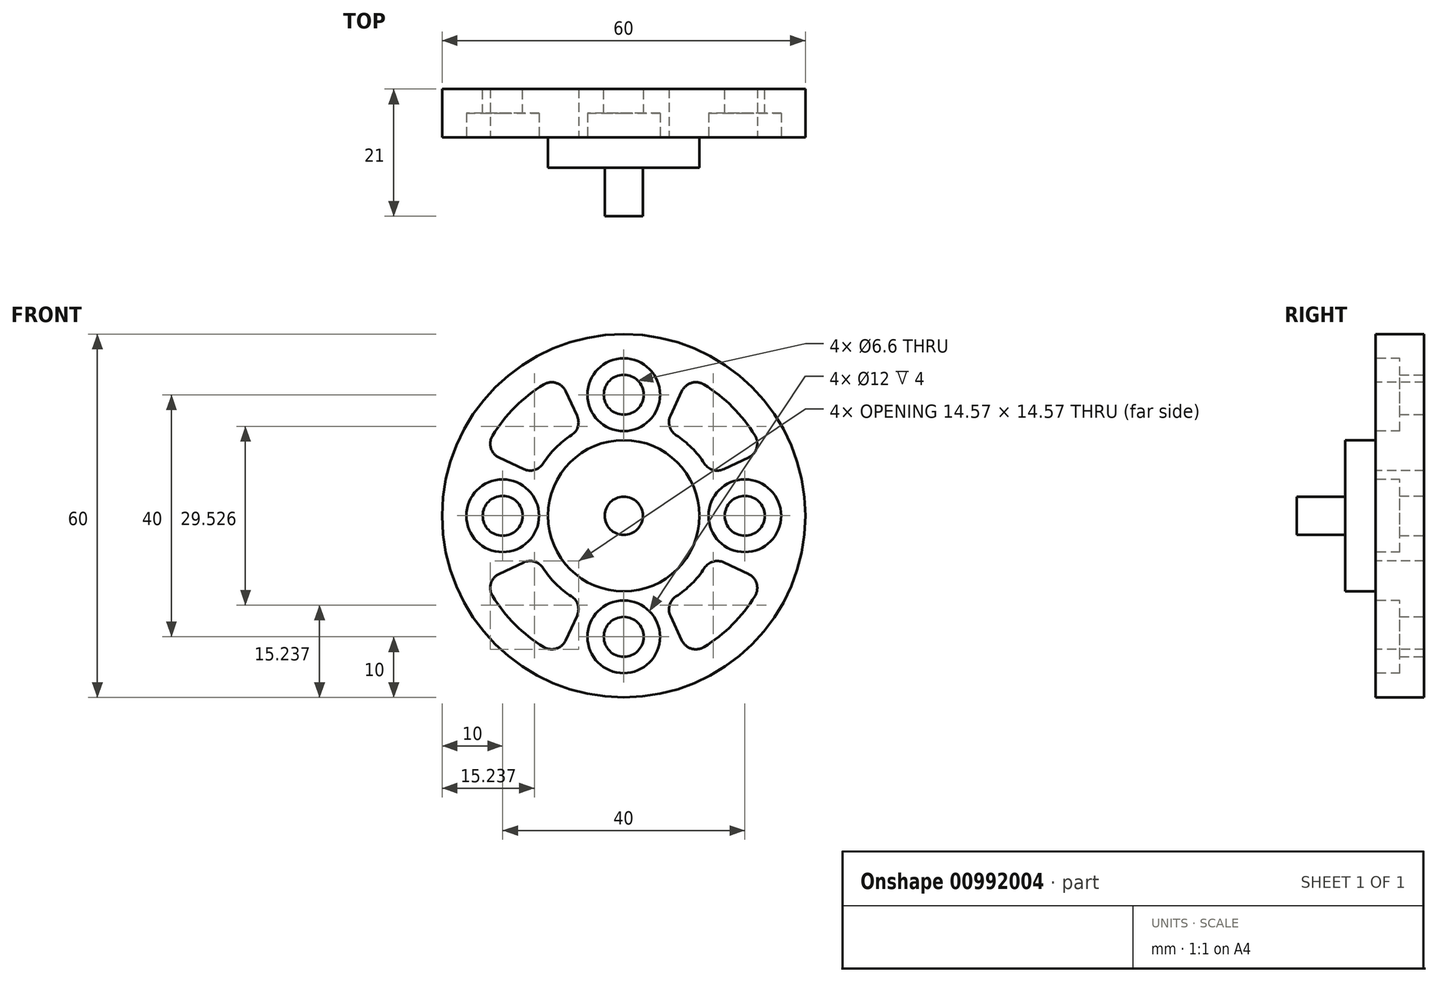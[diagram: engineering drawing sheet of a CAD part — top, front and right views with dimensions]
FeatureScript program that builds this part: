
annotation { "Feature Type Name" : "Feature", "Feature Type Description" : "" }
export const myFeature = defineFeature(function(context is Context, id is Id, definition is map)
    precondition{}
    {
        {
            var Q0;
            Q0=qCreatedBy(makeId("Front.planeOp"),FACE);
            var sketch = newSketch(context, id + "F0", { "sketchPlane" : qUnion([Q0])});
            skCircle(sketch, "E0", {"center": v(0, 0) * mm, "radius": 30 * mm});
            skCircle(sketch, "E1", {"center": v(0, 20) * mm, "radius": 3.3 * mm});
            skCircle(sketch, "E2", {"center": v(0, 0) * mm, "radius": 20 * mm, "construction": true});
            skCircle(sketch, "E3.1.0", {"center": v(-20, 0) * mm, "radius": 3.3 * mm});
            skCircle(sketch, "E3.2.0", {"center": v(0, -20) * mm, "radius": 3.3 * mm});
            skCircle(sketch, "E3.3.0", {"center": v(20, 0) * mm, "radius": 3.3 * mm});
            skSolve(sketch);
        }
        {
            var Q0;
            Q0=makeQuery(id+"F0.imprint","IMPRINT",FACE,{"disambiguationData":[TD([[makeQuery(id+"F0.imprint","IMPRINT",EDGE,{"derivedFrom":sQuery(id+"F0.wireOp",EDGE,"E0")}),1.0]])]});
            extrude(context, id + "F1", {"entities" : qUnion([Q0]), "depth" : 8 * mm, "offsetDistance" : 25.4 * mm});
        }
        {
            var Q0;
            Q0=makeQuery(id+"F1.opExtrude","CAP_FACE",FACE,{"disambiguationData":[OSD([sQuery(id+"F0.wireOp",EDGE,"E0"),sQuery(id+"F0.wireOp",EDGE,"E1"),sQuery(id+"F0.wireOp",EDGE,"E3.1.0"),sQuery(id+"F0.wireOp",EDGE,"E3.2.0"),sQuery(id+"F0.wireOp",EDGE,"E3.3.0")])],"isStart":false});
            var sketch = newSketch(context, id + "F2", { "sketchPlane" : qUnion([Q0])});
            skCircle(sketch, "E4", {"center": v(0, 20) * mm, "radius": 6 * mm});
            skCircle(sketch, "E5", {"center": v(-20, 0) * mm, "radius": 6 * mm});
            skCircle(sketch, "E6", {"center": v(20, 0) * mm, "radius": 6 * mm});
            skCircle(sketch, "E7", {"center": v(0, -20) * mm, "radius": 6 * mm});
            skSolve(sketch);
        }
        {
            var Q0;
            Q0 = qSketchRegion(id + "F2", true);
            extrude(context, id + "F3", {"entities" : qUnion([Q0]), "operationType" : NewBodyOperationType.REMOVE, "oppositeDirection" : true, "depth" : 4 * mm, "offsetDistance" : 25.4 * mm});
        }
        {
            var Q0;
            Q0=makeQuery(id+"F1.opExtrude","CAP_FACE",FACE,{"disambiguationData":[OSD([sQuery(id+"F0.wireOp",EDGE,"E0"),sQuery(id+"F0.wireOp",EDGE,"E1"),sQuery(id+"F0.wireOp",EDGE,"E3.1.0"),sQuery(id+"F0.wireOp",EDGE,"E3.2.0"),sQuery(id+"F0.wireOp",EDGE,"E3.3.0")])],"isStart":false});
            var sketch = newSketch(context, id + "F4", { "sketchPlane" : qUnion([Q0])});
            skCircle(sketch, "E8", {"center": v(0, 0) * mm, "radius": 12.5 * mm});
            skSolve(sketch);
        }
        {
            var Q0;
            Q0 = qSketchRegion(id + "F4", true);
            extrude(context, id + "F5", {"entities" : qUnion([Q0]), "operationType" : NewBodyOperationType.ADD, "depth" : 5 * mm, "offsetDistance" : 25.4 * mm});
        }
        {
            var Q0;
            Q0=makeQuery(id+"F5.opExtrude","CAP_FACE",FACE,{"disambiguationData":[OSD([sQuery(id+"F4.wireOp",EDGE,"E8")])],"isStart":false});
            var sketch = newSketch(context, id + "F6", { "sketchPlane" : qUnion([Q0])});
            skCircle(sketch, "E9", {"center": v(0, 0) * mm, "radius": 3.15 * mm});
            skSolve(sketch);
        }
        {
            var Q0;
            Q0 = qSketchRegion(id + "F6", true);
            extrude(context, id + "F7", {"entities" : qUnion([Q0]), "operationType" : NewBodyOperationType.ADD, "depth" : 8 * mm, "offsetDistance" : 25.4 * mm});
        }
        {
            var Q0;
            Q0=makeQuery(id+"F1.opExtrude","CAP_FACE",FACE,{"disambiguationData":[OSD([sQuery(id+"F0.wireOp",EDGE,"E0"),sQuery(id+"F0.wireOp",EDGE,"E1"),sQuery(id+"F0.wireOp",EDGE,"E3.1.0"),sQuery(id+"F0.wireOp",EDGE,"E3.2.0"),sQuery(id+"F0.wireOp",EDGE,"E3.3.0")])],"isStart":false});
            var sketch = newSketch(context, id + "F8", { "sketchPlane" : qUnion([Q0])});
            skArc(sketch, "E10", {"start": v(-8.63, 13.32) * mm, "mid": v(-11.23, 11.23) * mm, "end": v(-13.32, 8.63) * mm});
            skArc(sketch, "E11", {"start": v(-13.23, 21.68) * mm, "mid": v(-17.96, 17.96) * mm, "end": v(-21.68, 13.23) * mm});
            skLineSegment(sketch, "E12", {"start": v(-11.23, 11.23) * mm, "end": v(-17.96, 17.96) * mm, "construction": true});
            skLineSegment(sketch, "E13", {"start": v(0, 0) * mm, "end": v(-6.7, 14.39) * mm, "construction": true});
            skLineSegment(sketch, "E14", {"start": v(-9.6, 20.59) * mm, "end": v(-7.7, 16.53) * mm});
            skLineSegment(sketch, "E15.MirrorCS", {"start": v(-20.59, 9.6) * mm, "end": v(-16.53, 7.7) * mm});
            skPoint(sketch, "E16.visualSharp", {"position": v(-23.02, 10.73) * mm});
            skArc(sketch, "E16.filletArc", {"start": v(-21.68, 13.23) * mm, "mid": v(-21.95, 11.17) * mm, "end": v(-20.59, 9.6) * mm});
            skPoint(sketch, "E17.visualSharp", {"position": v(-10.73, 23.02) * mm});
            skArc(sketch, "E17.filletArc", {"start": v(-9.6, 20.59) * mm, "mid": v(-11.17, 21.95) * mm, "end": v(-13.23, 21.68) * mm});
            skPoint(sketch, "E18.visualSharp", {"position": v(-6.7, 14.39) * mm});
            skArc(sketch, "E18.filletArc", {"start": v(-8.63, 13.32) * mm, "mid": v(-7.57, 14.76) * mm, "end": v(-7.7, 16.53) * mm});
            skPoint(sketch, "E19.visualSharp", {"position": v(-14.39, 6.7) * mm});
            skArc(sketch, "E19.filletArc", {"start": v(-16.53, 7.7) * mm, "mid": v(-14.76, 7.57) * mm, "end": v(-13.32, 8.63) * mm});
            skArc(sketch, "E20.1.0", {"start": v(-21.68, -13.23) * mm, "mid": v(-17.96, -17.96) * mm, "end": v(-13.23, -21.68) * mm});
            skArc(sketch, "E20.1.1", {"start": v(-13.23, -21.68) * mm, "mid": v(-11.17, -21.95) * mm, "end": v(-9.6, -20.59) * mm});
            skLineSegment(sketch, "E20.1.2", {"start": v(-9.6, -20.59) * mm, "end": v(-7.7, -16.53) * mm});
            skPoint(sketch, "E20.1.3", {"position": v(-6.7, -14.39) * mm});
            skArc(sketch, "E20.1.4", {"start": v(-13.32, -8.63) * mm, "mid": v(-11.23, -11.23) * mm, "end": v(-8.63, -13.32) * mm});
            skArc(sketch, "E20.1.5", {"start": v(-13.32, -8.63) * mm, "mid": v(-14.76, -7.57) * mm, "end": v(-16.53, -7.7) * mm});
            skLineSegment(sketch, "E20.1.6", {"start": v(-20.59, -9.6) * mm, "end": v(-16.53, -7.7) * mm});
            skArc(sketch, "E20.1.7", {"start": v(-20.59, -9.6) * mm, "mid": v(-21.95, -11.17) * mm, "end": v(-21.68, -13.23) * mm});
            skArc(sketch, "E20.1.8", {"start": v(-7.7, -16.53) * mm, "mid": v(-7.57, -14.76) * mm, "end": v(-8.63, -13.32) * mm});
            skArc(sketch, "E20.2.0", {"start": v(13.23, -21.68) * mm, "mid": v(17.96, -17.96) * mm, "end": v(21.68, -13.23) * mm});
            skArc(sketch, "E20.2.1", {"start": v(21.68, -13.23) * mm, "mid": v(21.95, -11.17) * mm, "end": v(20.59, -9.6) * mm});
            skLineSegment(sketch, "E20.2.2", {"start": v(20.59, -9.6) * mm, "end": v(16.53, -7.7) * mm});
            skPoint(sketch, "E20.2.3", {"position": v(14.39, -6.7) * mm});
            skArc(sketch, "E20.2.4", {"start": v(8.63, -13.32) * mm, "mid": v(11.23, -11.23) * mm, "end": v(13.32, -8.63) * mm});
            skArc(sketch, "E20.2.5", {"start": v(8.63, -13.32) * mm, "mid": v(7.57, -14.76) * mm, "end": v(7.7, -16.53) * mm});
            skLineSegment(sketch, "E20.2.6", {"start": v(9.6, -20.59) * mm, "end": v(7.7, -16.53) * mm});
            skArc(sketch, "E20.2.7", {"start": v(9.6, -20.59) * mm, "mid": v(11.17, -21.95) * mm, "end": v(13.23, -21.68) * mm});
            skArc(sketch, "E20.2.8", {"start": v(16.53, -7.7) * mm, "mid": v(14.76, -7.57) * mm, "end": v(13.32, -8.63) * mm});
            skArc(sketch, "E20.3.0", {"start": v(21.68, 13.23) * mm, "mid": v(17.96, 17.96) * mm, "end": v(13.23, 21.68) * mm});
            skArc(sketch, "E20.3.1", {"start": v(13.23, 21.68) * mm, "mid": v(11.17, 21.95) * mm, "end": v(9.6, 20.59) * mm});
            skLineSegment(sketch, "E20.3.2", {"start": v(9.6, 20.59) * mm, "end": v(7.7, 16.53) * mm});
            skPoint(sketch, "E20.3.3", {"position": v(6.7, 14.39) * mm});
            skArc(sketch, "E20.3.4", {"start": v(13.32, 8.63) * mm, "mid": v(11.23, 11.23) * mm, "end": v(8.63, 13.32) * mm});
            skArc(sketch, "E20.3.5", {"start": v(13.32, 8.63) * mm, "mid": v(14.76, 7.57) * mm, "end": v(16.53, 7.7) * mm});
            skLineSegment(sketch, "E20.3.6", {"start": v(20.59, 9.6) * mm, "end": v(16.53, 7.7) * mm});
            skArc(sketch, "E20.3.7", {"start": v(20.59, 9.6) * mm, "mid": v(21.95, 11.17) * mm, "end": v(21.68, 13.23) * mm});
            skArc(sketch, "E20.3.8", {"start": v(7.7, 16.53) * mm, "mid": v(7.57, 14.76) * mm, "end": v(8.63, 13.32) * mm});
            skSolve(sketch);
        }
        {
            var Q0;
            Q0 = qSketchRegion(id + "F8", true);
            extrude(context, id + "F9", {"entities" : qUnion([Q0]), "operationType" : NewBodyOperationType.REMOVE, "oppositeDirection" : true, "depth" : 25.4 * mm, "offsetDistance" : 25.4 * mm});
        }
    });
